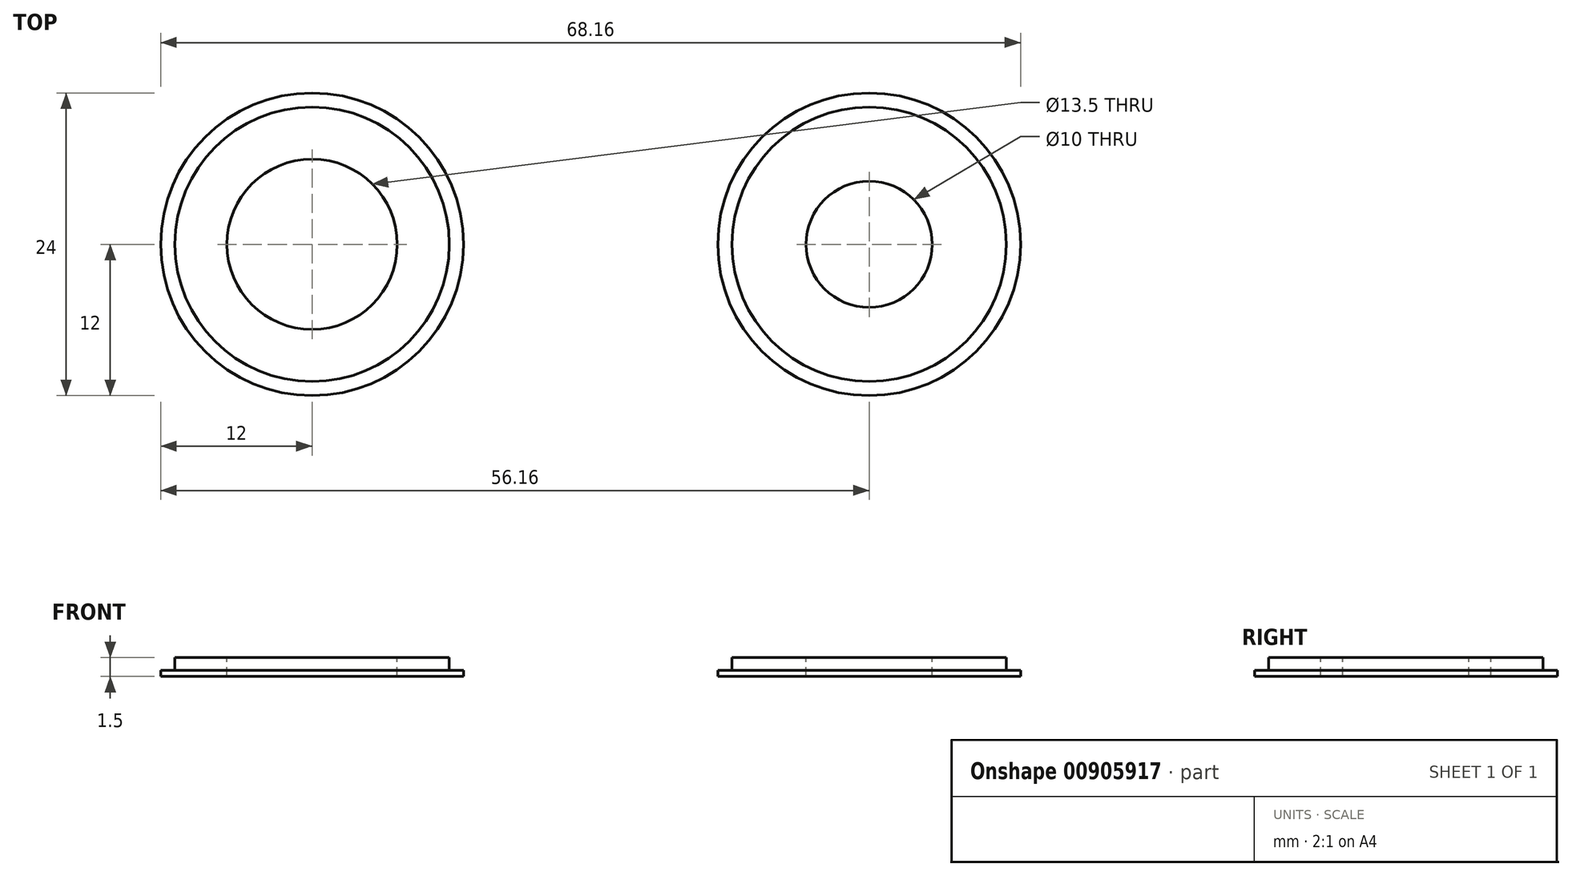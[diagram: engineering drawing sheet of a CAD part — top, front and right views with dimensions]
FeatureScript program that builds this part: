
annotation { "Feature Type Name" : "Feature", "Feature Type Description" : "" }
export const myFeature = defineFeature(function(context is Context, id is Id, definition is map)
    precondition{}
    {
        {
            var Q0;
            Q0=qCreatedBy(makeId("Top.planeOp"),FACE);
            var sketch = newSketch(context, id + "F0", { "sketchPlane" : qUnion([Q0])});
            skCircle(sketch, "E0", {"center": v(0, 0) * mm, "radius": 5 * mm});
            skCircle(sketch, "E1", {"center": v(0, 0) * mm, "radius": 10.88 * mm});
            skCircle(sketch, "E2", {"center": v(0, 0) * mm, "radius": 12 * mm});
            skCircle(sketch, "E3", {"center": v(-44.16, 0) * mm, "radius": 6.75 * mm});
            skCircle(sketch, "E4", {"center": v(-44.16, 0) * mm, "radius": 10.88 * mm});
            skCircle(sketch, "E5", {"center": v(-44.16, 0) * mm, "radius": 12 * mm});
            skSolve(sketch);
        }
        {
            var Q0;
            Q0=makeQuery(id+"F0.imprint","IMPRINT",FACE,{"disambiguationData":[TD([[makeQuery(id+"F0.imprint","IMPRINT",EDGE,{"derivedFrom":sQuery(id+"F0.wireOp",EDGE,"E0")}),-1.0]])]});
            var Q1;
            Q1=makeQuery(id+"F0.imprint","IMPRINT",FACE,{"disambiguationData":[TD([[makeQuery(id+"F0.imprint","IMPRINT",EDGE,{"derivedFrom":sQuery(id+"F0.wireOp",EDGE,"E1")}),-1.0]])]});
            extrude(context, id + "F1", {"entities" : qUnion([Q0, Q1]), "depth" : -0.5 * mm, "offsetDistance" : 25 * mm});
        }
        {
            var Q0;
            Q0=makeQuery(id+"F0.imprint","IMPRINT",FACE,{"disambiguationData":[TD([[makeQuery(id+"F0.imprint","IMPRINT",EDGE,{"derivedFrom":sQuery(id+"F0.wireOp",EDGE,"E0")}),-1.0]])]});
            extrude(context, id + "F2", {"entities" : qUnion([Q0]), "operationType" : NewBodyOperationType.ADD, "depth" : 1 * mm, "offsetDistance" : 25 * mm});
        }
        {
            var Q0;
            Q0=makeQuery(id+"F0.imprint","IMPRINT",FACE,{"disambiguationData":[TD([[makeQuery(id+"F0.imprint","IMPRINT",EDGE,{"derivedFrom":sQuery(id+"F0.wireOp",EDGE,"E3")}),-1.0]])]});
            var Q1;
            Q1=makeQuery(id+"F0.imprint","IMPRINT",FACE,{"disambiguationData":[TD([[makeQuery(id+"F0.imprint","IMPRINT",EDGE,{"derivedFrom":sQuery(id+"F0.wireOp",EDGE,"E4")}),-1.0]])]});
            extrude(context, id + "F3", {"entities" : qUnion([Q0, Q1]), "depth" : -0.5 * mm, "offsetDistance" : 25 * mm});
        }
        {
            var Q0;
            Q0=makeQuery(id+"F0.imprint","IMPRINT",FACE,{"disambiguationData":[TD([[makeQuery(id+"F0.imprint","IMPRINT",EDGE,{"derivedFrom":sQuery(id+"F0.wireOp",EDGE,"E3")}),-1.0]])]});
            extrude(context, id + "F4", {"entities" : qUnion([Q0]), "operationType" : NewBodyOperationType.ADD, "depth" : 1 * mm, "offsetDistance" : 25 * mm});
        }
    });
